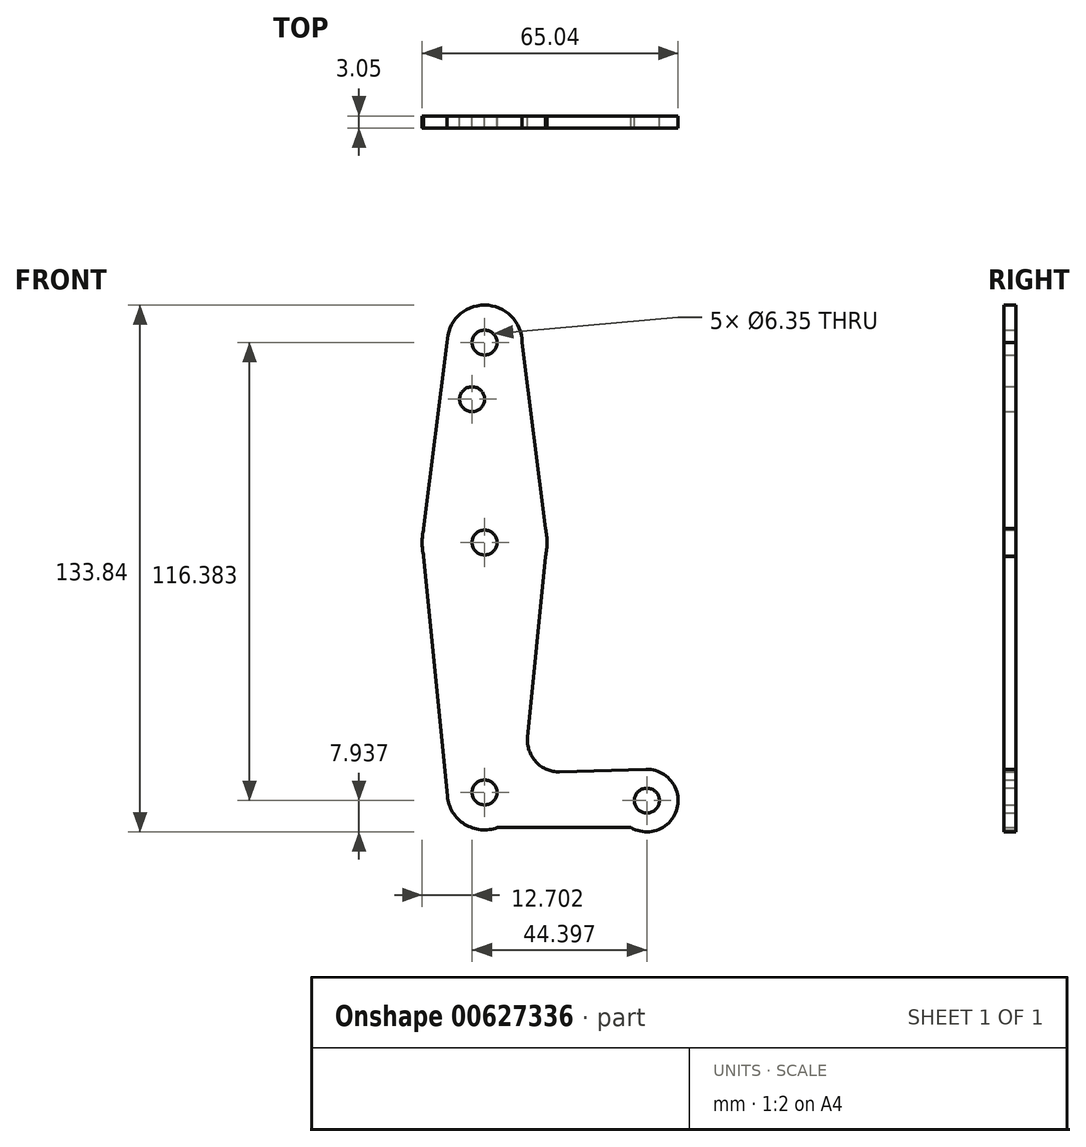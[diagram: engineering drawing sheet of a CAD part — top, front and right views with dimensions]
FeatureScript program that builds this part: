
annotation { "Feature Type Name" : "Feature", "Feature Type Description" : "" }
export const myFeature = defineFeature(function(context is Context, id is Id, definition is map)
    precondition{}
    {
        {
            var Q0;
            Q0=qCreatedBy(makeId("Front.planeOp"),FACE);
            var sketch = newSketch(context, id + "F0", { "sketchPlane" : qUnion([Q0])});
            skLineSegment(sketch, "E0", {"start": v(-15.7, 89.2) * mm, "end": v(-15.7, -25.1) * mm});
            skCircle(sketch, "E1", {"center": v(-15.7, -25.1) * mm, "radius": 9.53 * mm});
            skCircle(sketch, "E2", {"center": v(25.52, -27.18) * mm, "radius": 7.94 * mm});
            skCircle(sketch, "E3", {"center": v(-15.7, 38.4) * mm, "radius": 15.88 * mm});
            skLineSegment(sketch, "E4", {"start": v(-31.57, 38.83) * mm, "end": v(-25.18, -26.03) * mm});
            skLineSegment(sketch, "E5", {"start": v(0.17, 38.83) * mm, "end": v(-4.76, -11.15) * mm});
            skCircle(sketch, "E6", {"center": v(25.52, -27.18) * mm, "radius": 3.18 * mm});
            skCircle(sketch, "E7", {"center": v(-15.7, -25.1) * mm, "radius": 3.18 * mm});
            skCircle(sketch, "E8", {"center": v(-15.7, 38.4) * mm, "radius": 3.18 * mm});
            skCircle(sketch, "E9", {"center": v(-15.7, 89.2) * mm, "radius": 9.53 * mm});
            skLineSegment(sketch, "E10", {"start": v(-25.23, 89.2) * mm, "end": v(-31.57, 38.83) * mm});
            skLineSegment(sketch, "E11", {"start": v(-6.18, 89.2) * mm, "end": v(0.17, 38.83) * mm});
            skLineSegment(sketch, "E12", {"start": v(-19.02, -34.03) * mm, "end": v(21.5, -34.03) * mm});
            skLineSegment(sketch, "E13", {"start": v(24.72, -34.03) * mm, "end": v(24.78, -34.06) * mm});
            skCircle(sketch, "E14", {"center": v(-15.7, 89.2) * mm, "radius": 3.18 * mm});
            skLineSegment(sketch, "E15", {"start": v(3.38, -19.88) * mm, "end": v(25.52, -19.24) * mm});
            skPoint(sketch, "E16.newPointA", {"position": v(-15.7, -20.43) * mm});
            skPoint(sketch, "E16.newPointB", {"position": v(-6.22, -26.03) * mm});
            skArc(sketch, "E16.filletArc", {"start": v(-4.76, -11.15) * mm, "mid": v(-2.66, -17.36) * mm, "end": v(3.38, -19.88) * mm});
            skCircle(sketch, "E17", {"center": v(-18.88, 74.79) * mm, "radius": 3.18 * mm});
            skSolve(sketch);
        }
        {
            var Q0;
            Q0 = qSketchRegion(id + "F0", true);
            var Q1;
            {var subQ3=sQuery(id+"F0.wireOp",EDGE,"Mqut2IZM-UXOk-xy8l-IW0Z-UGozX49vrsEz");var subQ5=sQuery(id+"F0.wireOp",EDGE,"SQACIGv1-9YJh-wfX6-3sHy-l1RMm5UgnO1u");var subQ6=makeQuery(id+"F0.imprint","INTERSECT",VERTEX,{"derivedFrom":[subQ5,subQ3]});Q1=makeQuery(id+"F0.imprint","IMPRINT",FACE,{"disambiguationData":[TD([[makeQuery(id+"F0.imprint","IMPRINT",EDGE,{"disambiguationData":[TD([[subQ6,-1.0]])],"derivedFrom":subQ5}),1.0]])]});}
            extrude(context, id + "F1", {"entities" : qUnion([Q0, Q1]), "depth" : 3.05 * mm, "offsetDistance" : 25.4 * mm});
        }
    });
